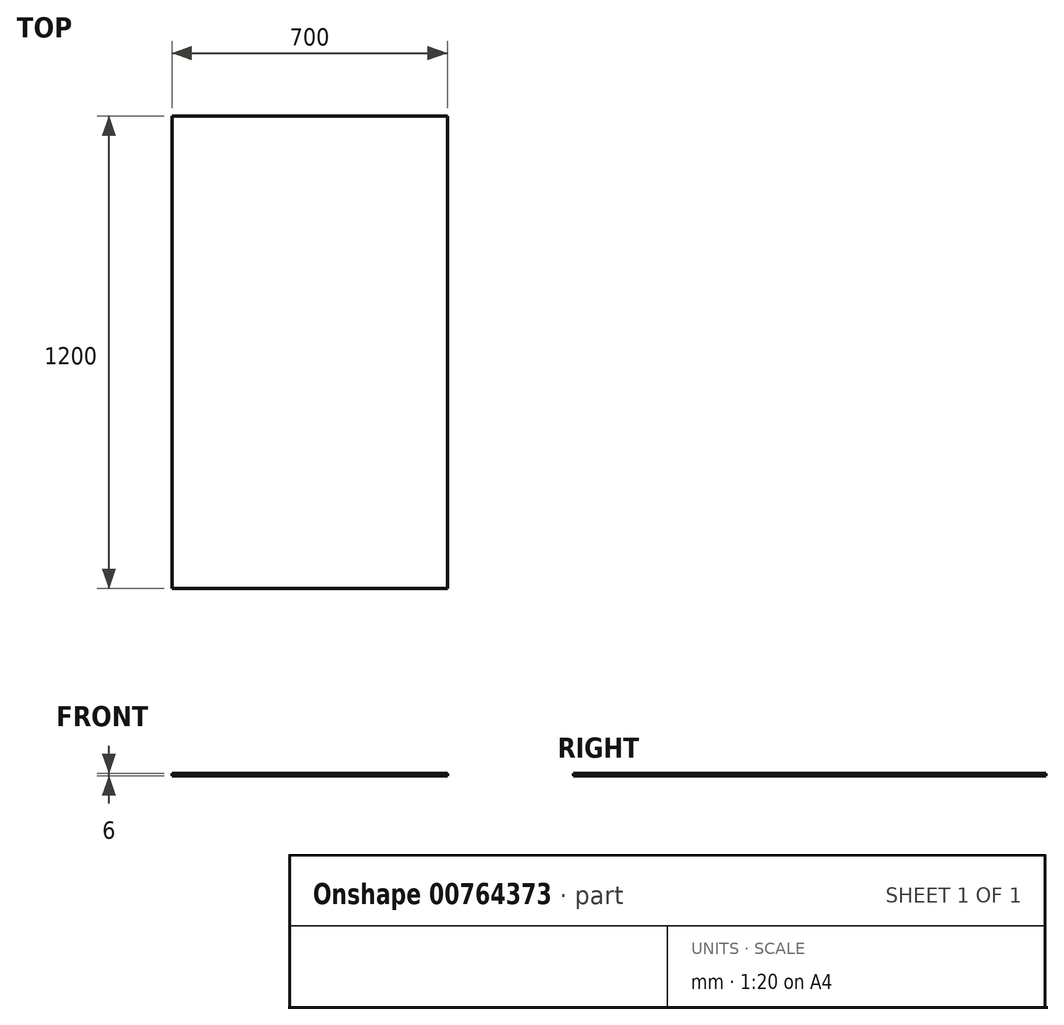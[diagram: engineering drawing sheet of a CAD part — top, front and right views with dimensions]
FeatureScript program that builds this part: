
annotation { "Feature Type Name" : "Feature", "Feature Type Description" : "" }
export const myFeature = defineFeature(function(context is Context, id is Id, definition is map)
    precondition{}
    {
        {
            var Q0;
            Q0=qCreatedBy(makeId("Front.planeOp"),FACE);
            var sketch = newSketch(context, id + "F0", { "sketchPlane" : qUnion([Q0])});
            skLineSegment(sketch, "E0.bottom", {"start": v(-350, 3) * mm, "end": v(350, 3) * mm});
            skLineSegment(sketch, "E0.top", {"start": v(-350, -3) * mm, "end": v(350, -3) * mm});
            skLineSegment(sketch, "E0.left", {"start": v(-350, 3) * mm, "end": v(-350, -3) * mm});
            skLineSegment(sketch, "E0.right", {"start": v(350, 3) * mm, "end": v(350, -3) * mm});
            skSolve(sketch);
        }
        {
            var Q0;
            Q0=makeQuery(id+"F0.imprint","IMPRINT",FACE,{"disambiguationData":[TD([[makeQuery(id+"F0.imprint","IMPRINT",EDGE,{"derivedFrom":sQuery(id+"F0.wireOp",EDGE,"E0.bottom")}),-1.0]])]});
            extrude(context, id + "F1", {"entities" : qUnion([Q0]), "depth" : 1200 * mm, "offsetDistance" : 25 * mm, "symmetric" : true});
        }
    });
